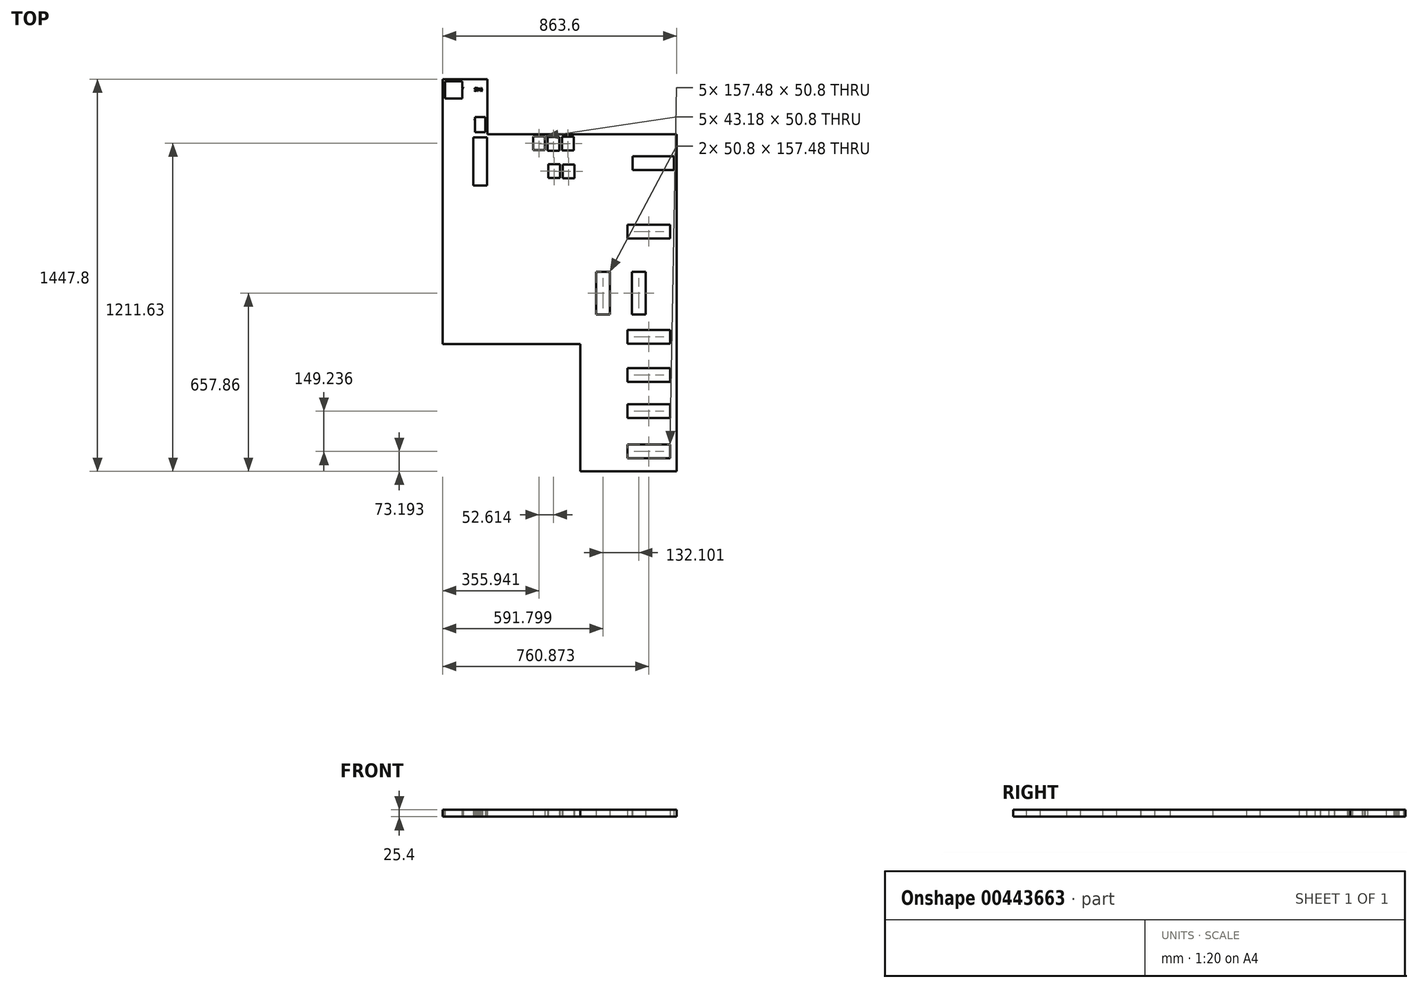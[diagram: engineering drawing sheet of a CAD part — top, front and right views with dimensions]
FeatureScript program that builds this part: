
annotation { "Feature Type Name" : "Feature", "Feature Type Description" : "" }
export const myFeature = defineFeature(function(context is Context, id is Id, definition is map)
    precondition{}
    {
        {
            var Q0;
            Q0=qCreatedBy(makeId("Top.planeOp"),FACE);
            var sketch = newSketch(context, id + "F0", { "sketchPlane" : qUnion([Q0])});
            skLineSegment(sketch, "E0", {"start": v(0, 0) * mm, "end": v(165.1, 0) * mm});
            skLineSegment(sketch, "E1", {"start": v(165.1, 0) * mm, "end": v(165.1, -203.2) * mm});
            skLineSegment(sketch, "E2", {"start": v(165.1, -203.2) * mm, "end": v(863.6, -203.2) * mm});
            skLineSegment(sketch, "E3", {"start": v(863.6, -203.2) * mm, "end": v(863.6, -1447.8) * mm});
            skLineSegment(sketch, "E4", {"start": v(863.6, -1447.8) * mm, "end": v(508, -1447.8) * mm});
            skLineSegment(sketch, "E5", {"start": v(508, -1447.8) * mm, "end": v(508, -977.9) * mm});
            skLineSegment(sketch, "E6", {"start": v(508, -977.9) * mm, "end": v(0, -977.9) * mm});
            skLineSegment(sketch, "E7", {"start": v(0, -977.9) * mm, "end": v(0, 0) * mm});
            skLineSegment(sketch, "E8", {"start": v(863.6, -203.2) * mm, "end": v(533.4, -203.2) * mm});
            skLineSegment(sketch, "E9", {"start": v(533.4, -203.2) * mm, "end": v(533.4, -457.2) * mm});
            skLineSegment(sketch, "E10", {"start": v(533.4, -457.2) * mm, "end": v(863.6, -457.2) * mm});
            skLineSegment(sketch, "E11", {"start": v(533.4, -457.2) * mm, "end": v(533.4, -711.2) * mm});
            skLineSegment(sketch, "E12", {"start": v(533.4, -711.2) * mm, "end": v(863.6, -711.2) * mm});
            skLineSegment(sketch, "E13", {"start": v(165.1, -203.2) * mm, "end": v(177.8, -203.2) * mm});
            skLineSegment(sketch, "E14", {"start": v(177.8, -203.2) * mm, "end": v(330.2, -203.2) * mm});
            skLineSegment(sketch, "E15", {"start": v(533.4, -457.2) * mm, "end": v(533.4, -444.5) * mm});
            skLineSegment(sketch, "E16", {"start": v(533.4, -444.5) * mm, "end": v(533.4, -368.3) * mm});
            skLineSegment(sketch, "E17.bottom", {"start": v(101.6, 0) * mm, "end": v(165.1, 0) * mm});
            skLineSegment(sketch, "E17.right", {"start": v(165.1, 0) * mm, "end": v(165.1, -63.5) * mm});
            skLineSegment(sketch, "E18.left", {"start": v(0, -776.35) * mm, "end": v(0, -819.53) * mm});
            skLineSegment(sketch, "E19.left", {"start": v(0, -824.22) * mm, "end": v(0, -867.4) * mm});
            skLineSegment(sketch, "E20.left", {"start": v(0, -873.94) * mm, "end": v(0, -824.22) * mm});
            skLineSegment(sketch, "E21.bottom", {"start": v(566.4, -711.2) * mm, "end": v(617.2, -711.2) * mm});
            skLineSegment(sketch, "E21.top", {"start": v(566.4, -868.68) * mm, "end": v(617.2, -868.68) * mm});
            skLineSegment(sketch, "E21.left", {"start": v(566.4, -711.2) * mm, "end": v(566.4, -868.68) * mm});
            skLineSegment(sketch, "E21.right", {"start": v(617.2, -711.2) * mm, "end": v(617.2, -868.68) * mm});
            skLineSegment(sketch, "E22.bottom", {"start": v(698.5, -711.2) * mm, "end": v(749.3, -711.2) * mm});
            skLineSegment(sketch, "E22.top", {"start": v(698.5, -868.68) * mm, "end": v(749.3, -868.68) * mm});
            skLineSegment(sketch, "E22.left", {"start": v(698.5, -711.2) * mm, "end": v(698.5, -868.68) * mm});
            skLineSegment(sketch, "E22.right", {"start": v(749.3, -711.2) * mm, "end": v(749.3, -868.68) * mm});
            skLineSegment(sketch, "E23.bottom", {"start": v(839.61, -925.83) * mm, "end": v(682.13, -925.83) * mm});
            skLineSegment(sketch, "E23.top", {"start": v(839.61, -976.63) * mm, "end": v(682.13, -976.63) * mm});
            skLineSegment(sketch, "E23.left", {"start": v(839.61, -925.83) * mm, "end": v(839.61, -976.63) * mm});
            skLineSegment(sketch, "E23.right", {"start": v(682.13, -925.83) * mm, "end": v(682.13, -976.63) * mm});
            skLineSegment(sketch, "E24.bottom", {"start": v(839.61, -1199.97) * mm, "end": v(682.13, -1199.97) * mm});
            skLineSegment(sketch, "E24.top", {"start": v(839.61, -1250.77) * mm, "end": v(682.13, -1250.77) * mm});
            skLineSegment(sketch, "E24.left", {"start": v(839.61, -1199.97) * mm, "end": v(839.61, -1250.77) * mm});
            skLineSegment(sketch, "E24.right", {"start": v(682.13, -1199.97) * mm, "end": v(682.13, -1250.77) * mm});
            skLineSegment(sketch, "E25", {"start": v(-468.5, -283.87) * mm, "end": v(-460.58, -283.87) * mm});
            skLineSegment(sketch, "E26.bottom", {"start": v(700.98, -283.87) * mm, "end": v(853.38, -283.87) * mm});
            skLineSegment(sketch, "E26.top", {"start": v(700.98, -334.67) * mm, "end": v(853.38, -334.67) * mm});
            skLineSegment(sketch, "E26.left", {"start": v(700.98, -283.87) * mm, "end": v(700.98, -334.67) * mm});
            skLineSegment(sketch, "E26.right", {"start": v(853.38, -283.87) * mm, "end": v(853.38, -334.67) * mm});
            skLineSegment(sketch, "E27", {"start": v(839.61, -925.83) * mm, "end": v(839.61, -927.46) * mm});
            skLineSegment(sketch, "E28.bottom", {"start": v(839.61, -536.8) * mm, "end": v(839.61, -587.6) * mm});
            skLineSegment(sketch, "E28.top", {"start": v(682.13, -536.8) * mm, "end": v(682.13, -587.6) * mm});
            skLineSegment(sketch, "E28.left", {"start": v(839.61, -536.8) * mm, "end": v(682.13, -536.8) * mm});
            skLineSegment(sketch, "E28.right", {"start": v(839.61, -587.6) * mm, "end": v(682.13, -587.6) * mm});
            skLineSegment(sketch, "E29", {"start": v(839.61, -1250.77) * mm, "end": v(839.61, -1273.02) * mm});
            skLineSegment(sketch, "E30.bottom", {"start": v(839.61, -1066.54) * mm, "end": v(839.61, -1117.34) * mm});
            skLineSegment(sketch, "E30.top", {"start": v(682.13, -1066.54) * mm, "end": v(682.13, -1117.34) * mm});
            skLineSegment(sketch, "E30.left", {"start": v(839.61, -1066.54) * mm, "end": v(682.13, -1066.54) * mm});
            skLineSegment(sketch, "E30.right", {"start": v(839.61, -1117.34) * mm, "end": v(682.13, -1117.34) * mm});
            skLineSegment(sketch, "E31.bottom", {"start": v(682.13, -1349.2) * mm, "end": v(839.61, -1349.2) * mm});
            skLineSegment(sketch, "E31.top", {"start": v(682.13, -1400) * mm, "end": v(839.61, -1400) * mm});
            skLineSegment(sketch, "E31.left", {"start": v(682.13, -1349.2) * mm, "end": v(682.13, -1400) * mm});
            skLineSegment(sketch, "E31.right", {"start": v(839.61, -1349.2) * mm, "end": v(839.61, -1400) * mm});
            skLineSegment(sketch, "E32.bottom", {"start": v(112.53, -214.82) * mm, "end": v(163.33, -214.82) * mm});
            skLineSegment(sketch, "E32.top", {"start": v(112.53, -392.62) * mm, "end": v(163.33, -392.62) * mm});
            skLineSegment(sketch, "E32.left", {"start": v(112.53, -214.82) * mm, "end": v(112.53, -392.62) * mm});
            skLineSegment(sketch, "E32.right", {"start": v(163.33, -214.82) * mm, "end": v(163.33, -392.62) * mm});
            skLineSegment(sketch, "E33", {"start": v(165.1, -203.2) * mm, "end": v(0, -204.02) * mm});
            skArc(sketch, "E34", {"start": v(29.97, -156.34) * mm, "mid": v(14.5, -177.92) * mm, "end": v(9.34, -203.97) * mm});
            skLineSegment(sketch, "E35", {"start": v(29.97, -156.34) * mm, "end": v(72.03, -202.84) * mm});
            skLineSegment(sketch, "E36.bottom", {"start": v(99.06, -55.88) * mm, "end": v(99.06, 0) * mm});
            skLineSegment(sketch, "E36.top", {"start": v(165.1, -55.88) * mm, "end": v(165.1, 0) * mm});
            skLineSegment(sketch, "E36.left", {"start": v(99.06, -55.88) * mm, "end": v(165.1, -55.88) * mm});
            skLineSegment(sketch, "E36.right", {"start": v(99.06, 0) * mm, "end": v(165.1, 0) * mm});
            skLineSegment(sketch, "E37.bottom", {"start": v(157.37, -195.6) * mm, "end": v(119.27, -195.6) * mm});
            skLineSegment(sketch, "E37.top", {"start": v(157.37, -139.72) * mm, "end": v(119.27, -139.72) * mm});
            skLineSegment(sketch, "E37.left", {"start": v(157.37, -195.6) * mm, "end": v(157.37, -139.72) * mm});
            skLineSegment(sketch, "E37.right", {"start": v(119.27, -195.6) * mm, "end": v(119.27, -139.72) * mm});
            skLineSegment(sketch, "E38.bottom", {"start": v(8.95, -7.44) * mm, "end": v(72.45, -7.44) * mm});
            skLineSegment(sketch, "E38.top", {"start": v(8.95, -70.94) * mm, "end": v(72.45, -70.94) * mm});
            skLineSegment(sketch, "E38.left", {"start": v(8.95, -7.44) * mm, "end": v(8.95, -70.94) * mm});
            skLineSegment(sketch, "E38.right", {"start": v(72.45, -7.44) * mm, "end": v(72.45, -70.94) * mm});
            skText(sketch, "E39", { "text": "Toilet\n", "fontName": "OpenSans-Regular.ttf"});
            skText(sketch, "E40", { "text": "Sink", "fontName": "OpenSans-Regular.ttf"});
            skText(sketch, "E41", { "text": "Laundry\n", "fontName": "OpenSans-Regular.ttf"});
            skLineSegment(sketch, "E42", {"start": v(533.4, -368.3) * mm, "end": v(329.18, -368.3) * mm});
            skLineSegment(sketch, "E43.bottom", {"start": v(334.35, -210.77) * mm, "end": v(377.53, -210.77) * mm});
            skLineSegment(sketch, "E43.top", {"start": v(334.35, -261.57) * mm, "end": v(377.53, -261.57) * mm});
            skLineSegment(sketch, "E43.left", {"start": v(334.35, -210.77) * mm, "end": v(334.35, -261.57) * mm});
            skLineSegment(sketch, "E43.right", {"start": v(377.53, -210.77) * mm, "end": v(377.53, -261.57) * mm});
            skLineSegment(sketch, "E44.bottom", {"start": v(386.97, -212.66) * mm, "end": v(430.15, -212.66) * mm});
            skLineSegment(sketch, "E44.top", {"start": v(386.97, -263.46) * mm, "end": v(430.15, -263.46) * mm});
            skLineSegment(sketch, "E44.left", {"start": v(386.97, -212.66) * mm, "end": v(386.97, -263.46) * mm});
            skLineSegment(sketch, "E44.right", {"start": v(430.15, -212.66) * mm, "end": v(430.15, -263.46) * mm});
            skLineSegment(sketch, "E45.bottom", {"start": v(440.7, -211.82) * mm, "end": v(483.88, -211.82) * mm});
            skLineSegment(sketch, "E45.top", {"start": v(440.7, -262.62) * mm, "end": v(483.88, -262.62) * mm});
            skLineSegment(sketch, "E45.left", {"start": v(440.7, -211.82) * mm, "end": v(440.7, -262.62) * mm});
            skLineSegment(sketch, "E45.right", {"start": v(483.88, -211.82) * mm, "end": v(483.88, -262.62) * mm});
            skLineSegment(sketch, "E46.bottom", {"start": v(390.47, -313.84) * mm, "end": v(433.65, -313.84) * mm});
            skLineSegment(sketch, "E46.top", {"start": v(390.47, -364.64) * mm, "end": v(433.65, -364.64) * mm});
            skLineSegment(sketch, "E46.left", {"start": v(390.47, -313.84) * mm, "end": v(390.47, -364.64) * mm});
            skLineSegment(sketch, "E46.right", {"start": v(433.65, -313.84) * mm, "end": v(433.65, -364.64) * mm});
            skLineSegment(sketch, "E47.bottom", {"start": v(443.12, -315.17) * mm, "end": v(486.3, -315.17) * mm});
            skLineSegment(sketch, "E47.top", {"start": v(443.12, -365.97) * mm, "end": v(486.3, -365.97) * mm});
            skLineSegment(sketch, "E47.left", {"start": v(443.12, -315.17) * mm, "end": v(443.12, -365.97) * mm});
            skLineSegment(sketch, "E47.right", {"start": v(486.3, -315.17) * mm, "end": v(486.3, -365.97) * mm});
            const initialGuessF0  = {"E39": [0.11678, -0.16038, 1, 0, 0.01184], "E40": [0.11715, -0.04286, 1, 0, 0.01116], "E41": [0.00342, -0.03812, 1, 0, 0.01367]};
            skSetInitialGuess(sketch, initialGuessF0);
            skSolve(sketch);
        }
        {
            var Q0;
            Q0 = qSketchRegion(id + "F0", true);
            extrude(context, id + "F1", {"entities" : qUnion([Q0]), "depth" : 25.4 * mm});
        }
    });
